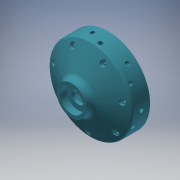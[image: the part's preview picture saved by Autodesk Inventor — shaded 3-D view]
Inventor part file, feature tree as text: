
AUTODESK INVENTOR PART (.ipt)
format: ipt  version: 2018 (Build 220112000, 112)  size: 406,528 bytes
history: native  units: mm
features: sketch x5, revolve x2, extrude x2, hole x1, other x1, pattern_circular x1, projected_geometry x1
ambient origin geometry x8: Origin, YZ Plane, XZ Plane, XY Plane, X Axis, Y Axis, Z Axis, Center Point
bodies: Solid1 (feature_tree)
feature tree (13):
  revolve  "Revolution1"  [1 undecoded]
  extrude  "Extrusion1"  Depth=6.0mm
  hole  "Hole1"  [1 undecoded]
  revolve  "Revolution2"  [1 undecoded]
  extrude  "Extrusion2"  Depth=10.0mm
  other  "Work Axis1"
  pattern_circular  "Circular Pattern1"  [2 undecoded]
  sketch  "Sketch1"  dims[d0=50.0mm d1=45.0mm]
  sketch  "Sketch2"  dims[d2=40.5mm d3=6.0mm]
  sketch  "Sketch3"  dims[d4=32.5mm d5=44.0mm]
  sketch  "Sketch4"  dims[d6=3.5mm d7=18.0mm]
  sketch  "Sketch5"  dims[d8=14.0mm d9=4.63734mm d10=8.0mm d11=3.5mm d12=8.0mm d13=3.0mm d14=90.0deg d15=5.0mm d16=7.0mm d17=9.0mm d18=10.0mm d19=16.5mm d20=59.5mm d21=0.0mm d23=4.0mm d24=6.0mm d25=4.0mm d26=2.0mm d27=90.0deg d28=24.5mm d29=0.0mm d30=3.5mm d32=5.0mm d33=90.0deg d34=70.0mm d35=360.0deg d37=21.0mm d38=42.5mm d39=5.0mm d40=10.0mm d41=0.0mm d42=22.5mm]
  projected_geometry  "Projected Loop1"
note: 5 required parameter values undecoded (feature->parameter linkage not recoverable at this tier; creation-order binding heuristic only, values carry confidence <= 0.55)